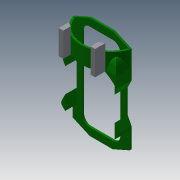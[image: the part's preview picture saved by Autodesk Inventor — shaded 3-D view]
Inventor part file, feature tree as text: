
AUTODESK INVENTOR PART (.ipt)
format: ipt  version: 2013 (Build 170138000, 138)  size: 681,984 bytes
history: native  units: mm
features: sketch x24, extrude x23, chamfer x3, fillet x2
ambient origin geometry x8: Origin, YZ Plane, XZ Plane, XY Plane, X Axis, Y Axis, Z Axis, Center Point
bodies: Solid1 (feature_tree)
feature tree (52):
  extrude  "Extrusion1"  Depth=4.0mm
  extrude  "Extrusion2"  Depth=4.0mm
  extrude  "Extrusion3"  Depth=4.0mm
  fillet  "Fillet1"  Radius=4.0mm
  extrude  "Extrusion4"  Depth=4.0mm
  extrude  "Extrusion5"  Depth=4.0mm
  extrude  "Extrusion6"  Depth=4.0mm
  sketch  "Sketch8"  dims[d13=4.0mm d14=4.0mm]
  extrude  "Extrusion7"  Depth=4.0mm
  extrude  "Extrusion8"  Depth=4.0mm
  extrude  "Extrusion9"  Depth=4.0mm
  extrude  "Extrusion10"  Depth=4.0mm
  extrude  "Extrusion11"  Depth=4.0mm
  extrude  "Extrusion12"  Depth=4.0mm
  extrude  "Extrusion13"  Depth=1.3mm TaperAngle=0.0deg
  extrude  "Extrusion14"  Depth=10.0mm
  extrude  "Extrusion15"  Depth=10.0mm
  extrude  "Extrusion16"  Depth=10.0mm
  extrude  "Extrusion17"  Depth=20.0mm
  extrude  "Extrusion18"  Depth=3.3mm TaperAngle=0.0deg
  extrude  "Extrusion19"  Depth=80.0mm
  extrude  "Extrusion20"  Depth=20.0mm TaperAngle=0.0deg
  chamfer  "Chamfer8"  Distance=30.0mm
  chamfer  "Chamfer9"  Distance=30.0mm
  chamfer  "Chamfer10"  Distance=35.0mm
  fillet  "Fillet6"  Radius=3.0mm
  extrude  "Extrusion21"  Depth=6.2mm TaperAngle=0.0deg
  extrude  "Extrusion22"  Depth=6.2mm TaperAngle=0.0deg
  extrude  "Extrusion23"  Depth=83.5mm
  sketch  "Sketch1"  dims[d0=4.0mm d1=4.0mm]
  sketch  "Sketch2"  dims[d2=4.0mm d3=4.0mm]
  sketch  "Sketch3"  dims[d4=4.0mm d5=4.0mm d6=4.0mm]
  sketch  "Sketch5"  dims[d7=4.0mm d8=4.0mm]
  sketch  "Sketch6"  dims[d9=4.0mm d10=4.0mm]
  sketch  "Sketch7"  dims[d11=4.0mm d12=4.0mm]
  sketch  "Sketch9"  dims[d15=4.0mm d16=4.0mm]
  sketch  "Sketch10"  dims[d17=4.0mm d18=4.0mm]
  sketch  "Sketch11"  dims[d19=4.0mm d20=4.0mm]
  sketch  "Sketch12"  dims[d21=4.0mm d22=4.0mm]
  sketch  "Sketch13"  dims[d23=4.0mm d24=4.0mm]
  sketch  "Sketch14"  dims[d25=2.0mm d26=0.0mm d27=1.3mm d28=0.0mm]
  sketch  "Sketch15"  dims[d29=10.0mm d30=10.0mm]
  sketch  "Sketch16"  dims[d31=10.0mm d32=10.0mm]
  sketch  "Sketch17"  dims[d33=10.0mm d34=10.0mm]
  sketch  "Sketch18"  dims[d35=3.3mm d36=0.0mm d37=20.0mm]
  sketch  "Sketch19"  dims[d38=3.0mm d39=0.0mm d40=3.3mm d41=0.0mm]
  sketch  "Sketch20"  dims[d42=1.7mm d43=0.0mm d46=80.0mm]
  sketch  "Sketch21"  dims[d47=65.0mm d48=0.0mm d49=20.0mm d50=0.0mm]
  sketch  "Sketch22"  dims[d51=53.0mm d52=30.0mm d53=0.0mm d54=30.0mm d55=0.0mm d56=35.0mm d57=0.0mm d58=3.0mm]
  sketch  "Sketch23"  dims[d59=3.0mm d61=6.2mm d62=0.0mm]
  sketch  "Sketch24"  dims[d63=35.0mm d64=0.0mm d84=6.2mm d85=0.0mm]
  sketch  "Sketch25"  dims[d86=30.0mm d87=0.0mm d88=83.5mm d89=30.0mm d90=0.0mm d91=35.0mm d92=0.0mm d93=3.0mm d94=3.0mm d95=5.0mm d96=0.0mm d97=35.0mm d98=0.0mm d99=1.2mm d100=0.0mm d107=12.85mm d108=2.0mm d109=45.0deg d110=10.0mm d111=2.0mm d112=45.0deg d113=10.0mm d114=2.0mm d115=45.0deg d116=21.0mm d117=8.0mm d119=30.0mm d120=0.0mm d121=82.6mm d123=5.0mm d130=7.0mm d131=28.0mm d132=45.0mm d133=0.0mm d134=20.0mm d135=0.0mm]
